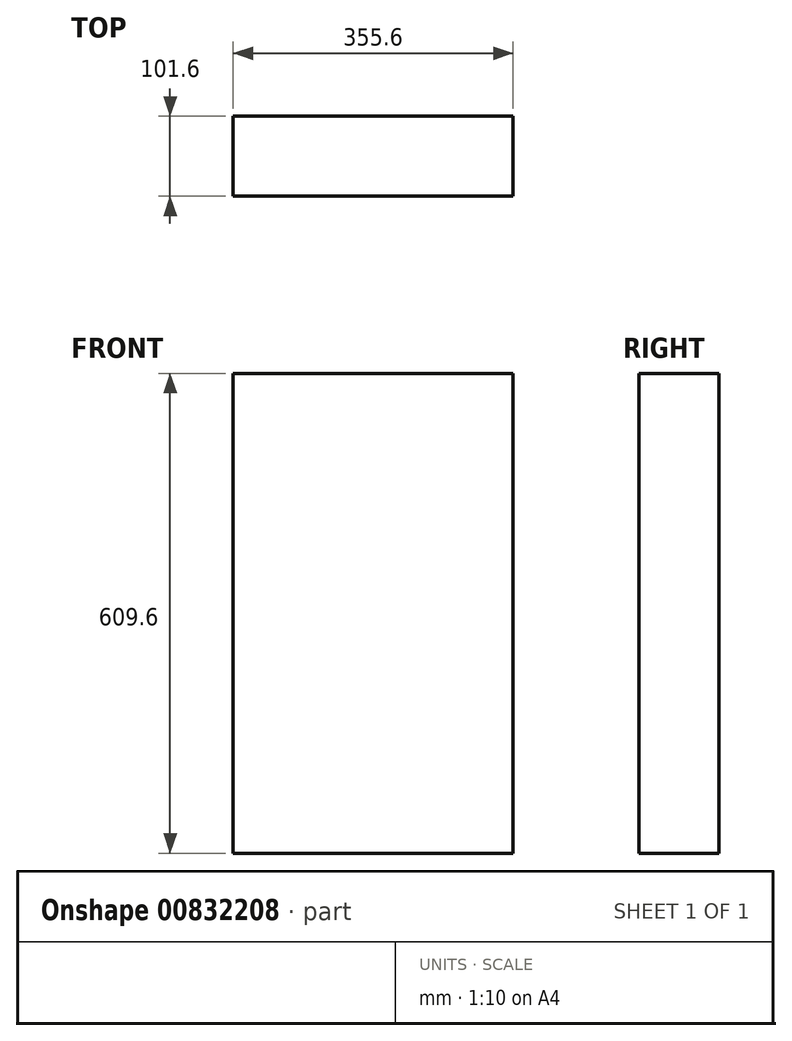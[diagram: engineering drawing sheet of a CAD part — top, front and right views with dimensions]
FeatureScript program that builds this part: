
annotation { "Feature Type Name" : "Feature", "Feature Type Description" : "" }
export const myFeature = defineFeature(function(context is Context, id is Id, definition is map)
    precondition{}
    {
        {
            var Q0;
            Q0=qCreatedBy(makeId("Front.planeOp"),FACE);
            var sketch = newSketch(context, id + "F0", { "sketchPlane" : qUnion([Q0])});
            skLineSegment(sketch, "E0.bottom", {"start": v(177.8, 304.8) * mm, "end": v(-177.8, 304.8) * mm});
            skLineSegment(sketch, "E0.top", {"start": v(177.8, -304.8) * mm, "end": v(-177.8, -304.8) * mm});
            skLineSegment(sketch, "E0.left", {"start": v(177.8, 304.8) * mm, "end": v(177.8, -304.8) * mm});
            skLineSegment(sketch, "E0.right", {"start": v(-177.8, 304.8) * mm, "end": v(-177.8, -304.8) * mm});
            skPoint(sketch, "E0.middle", {"position": v(0, 0) * mm});
            skSolve(sketch);
        }
        {
            var Q0;
            Q0=qSketchRegion(id+"F0",true);
            extrude(context, id + "F1", {"entities" : qUnion([Q0]), "depth" : 101.6 * mm, "offsetDistance" : 25.4 * mm});
        }
    });
